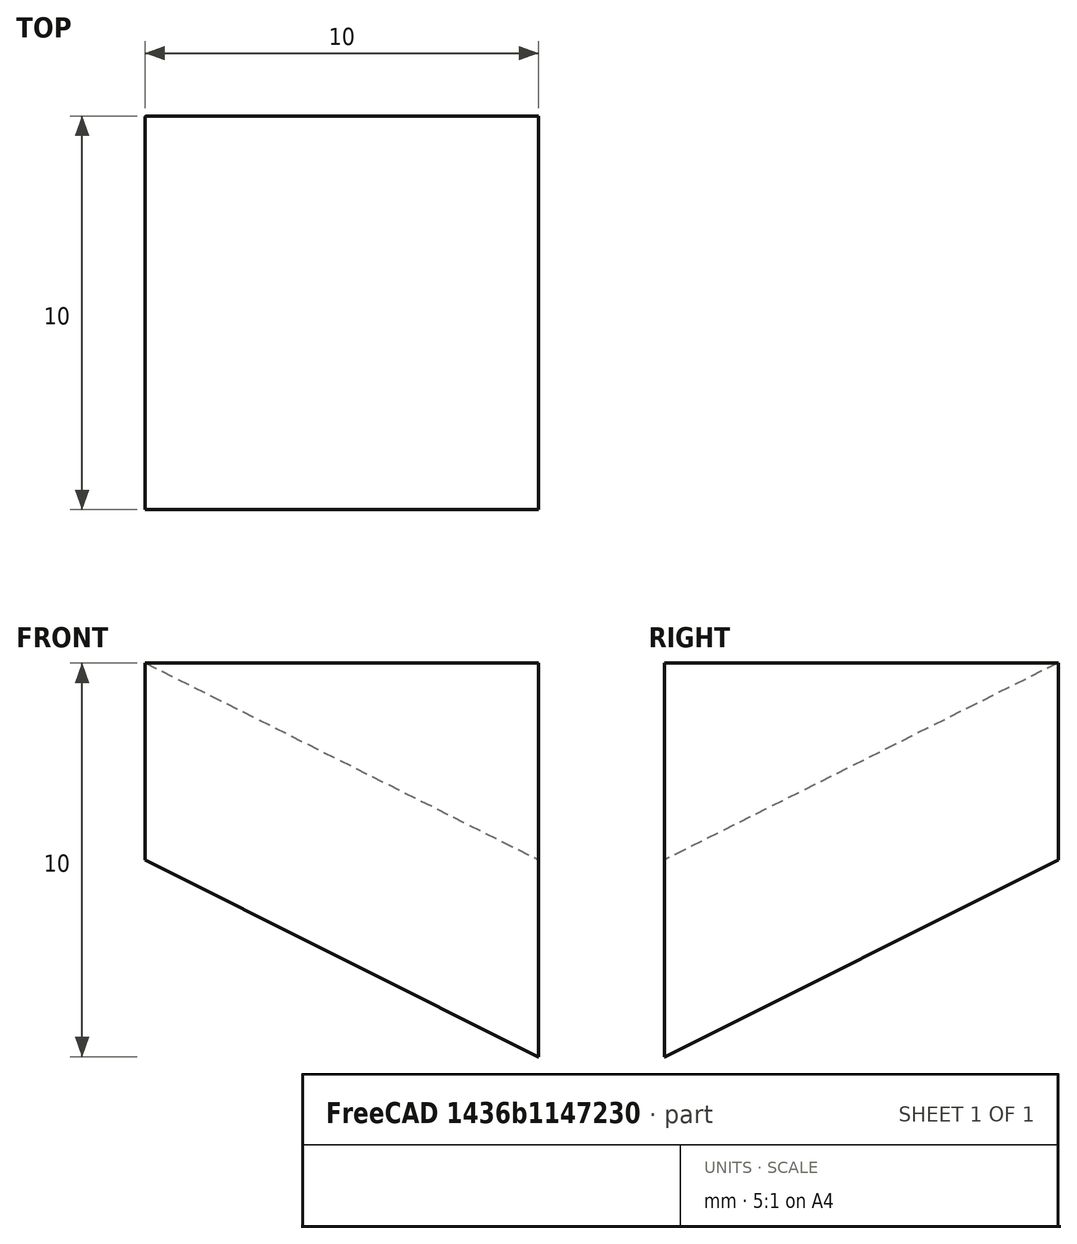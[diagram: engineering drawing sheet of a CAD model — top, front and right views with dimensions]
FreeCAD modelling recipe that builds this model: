
FCSTD DOCUMENT  (FreeCAD 0.18.3R)
Label: molcube-test
License: All rights reserved
LicenseURL: http://en.wikipedia.org/wiki/All_rights_reserved
objects: Part::Box×4, Part::Cut×1, Part::MultiCommon×1
note: 6 computed .brp shape members not serialized (recipe doc carries the construction recipe); baked Part::Feature solids carry a one-line shape summary decoded from their .brp

FEATURE [Part::Box] Box  label="Cube"
  AttacherType = Attacher::AttachEngine3D
  Height = 10
  Length = 10
  Placement = pos=(-5,-5,-5) rot=(0,0,1;0rad)
  Width = 10
FEATURE [Part::Box] Box001  label="Cube001"
  AttacherType = Attacher::AttachEngine3D
  Height = 30
  Length = 30
  Placement = pos=(-15,-15,0) rot=(0.707107,0.707107,0;0.616101rad)
  Width = 30
FEATURE [Part::Box] Box002  label="Cube002"
  AttacherType = Attacher::AttachEngine3D
  Height = 10
  Length = 10
  Placement = pos=(-5,-5,-5) rot=(0,0,1;0rad)
  Width = 10
FEATURE [Part::Box] Box003  label="Cube003"
  AttacherType = Attacher::AttachEngine3D
  Height = 30
  Length = 30
  Placement = pos=(-15,-15,0) rot=(0.707107,0.707107,0;0.616101rad)
  Width = 30
FEATURE [Part::Cut] Cut
  Base = -> Box
  Tool = -> Box001
FEATURE [Part::MultiCommon] Common
  Shapes = -> [Box002,Box003]
